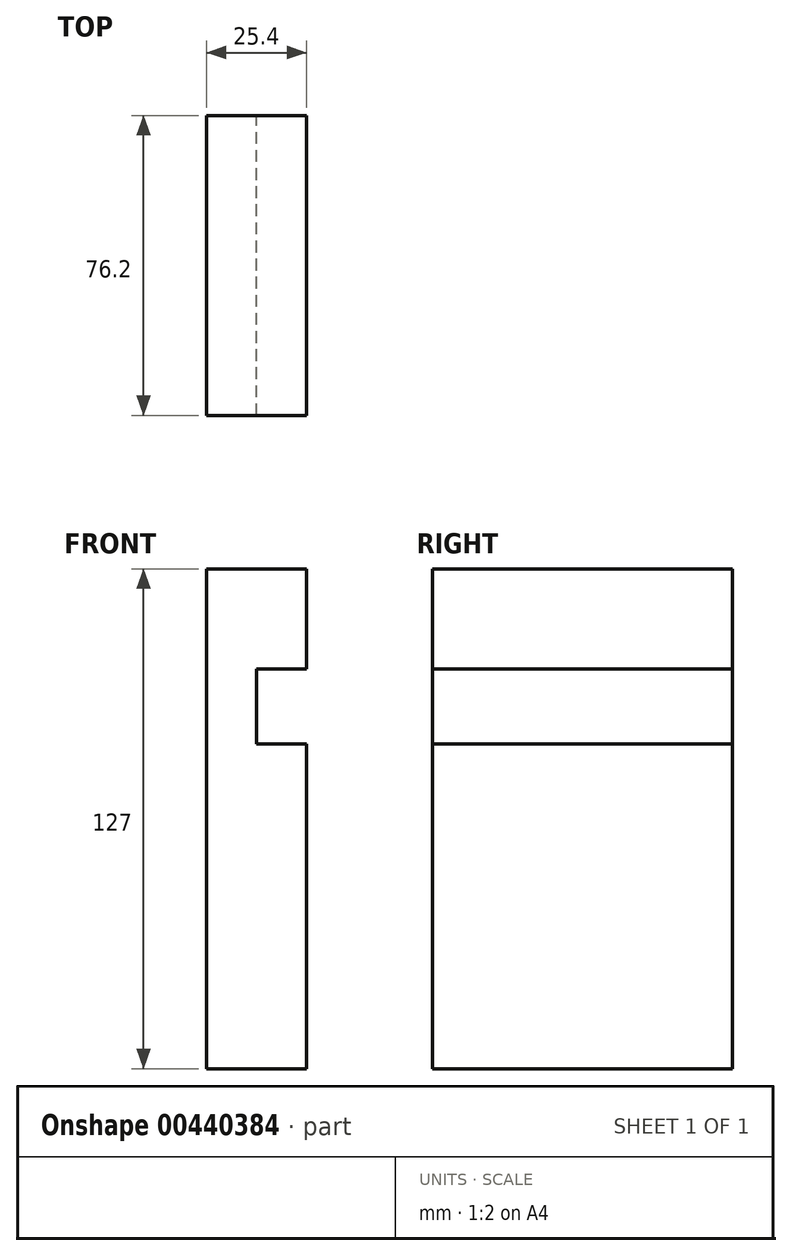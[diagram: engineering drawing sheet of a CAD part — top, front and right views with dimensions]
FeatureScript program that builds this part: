
annotation { "Feature Type Name" : "Feature", "Feature Type Description" : "" }
export const myFeature = defineFeature(function(context is Context, id is Id, definition is map)
    precondition{}
    {
        {
            var Q0;
            Q0=qCreatedBy(makeId("Front.planeOp"),FACE);
            var sketch = newSketch(context, id + "F0", { "sketchPlane" : qUnion([Q0])});
            skLineSegment(sketch, "E0", {"start": v(-38.92, -52.67) * mm, "end": v(-38.92, 74.33) * mm});
            skLineSegment(sketch, "E1", {"start": v(-38.92, 74.33) * mm, "end": v(-13.52, 74.33) * mm});
            skLineSegment(sketch, "E2", {"start": v(-13.52, 74.33) * mm, "end": v(-13.52, 48.93) * mm});
            skLineSegment(sketch, "E3", {"start": v(-13.52, 48.93) * mm, "end": v(-26.22, 48.93) * mm});
            skLineSegment(sketch, "E4", {"start": v(-26.22, 48.93) * mm, "end": v(-26.22, 29.88) * mm});
            skLineSegment(sketch, "E5", {"start": v(-26.22, 29.88) * mm, "end": v(-13.52, 29.88) * mm});
            skLineSegment(sketch, "E6", {"start": v(-13.52, 29.88) * mm, "end": v(-13.52, -52.67) * mm});
            skLineSegment(sketch, "E7", {"start": v(-13.52, -52.67) * mm, "end": v(-38.92, -52.67) * mm});
            skSolve(sketch);
        }
        {
            var Q0;
            Q0=makeQuery(id+"F0.imprint","IMPRINT",FACE,{"disambiguationData":[TD([[makeQuery(id+"F0.imprint","IMPRINT",EDGE,{"derivedFrom":sQuery(id+"F0.wireOp",EDGE,"E0")}),-1.0]])]});
            extrude(context, id + "F1", {"entities" : qUnion([Q0]), "depth" : 76.2 * mm});
        }
    });
